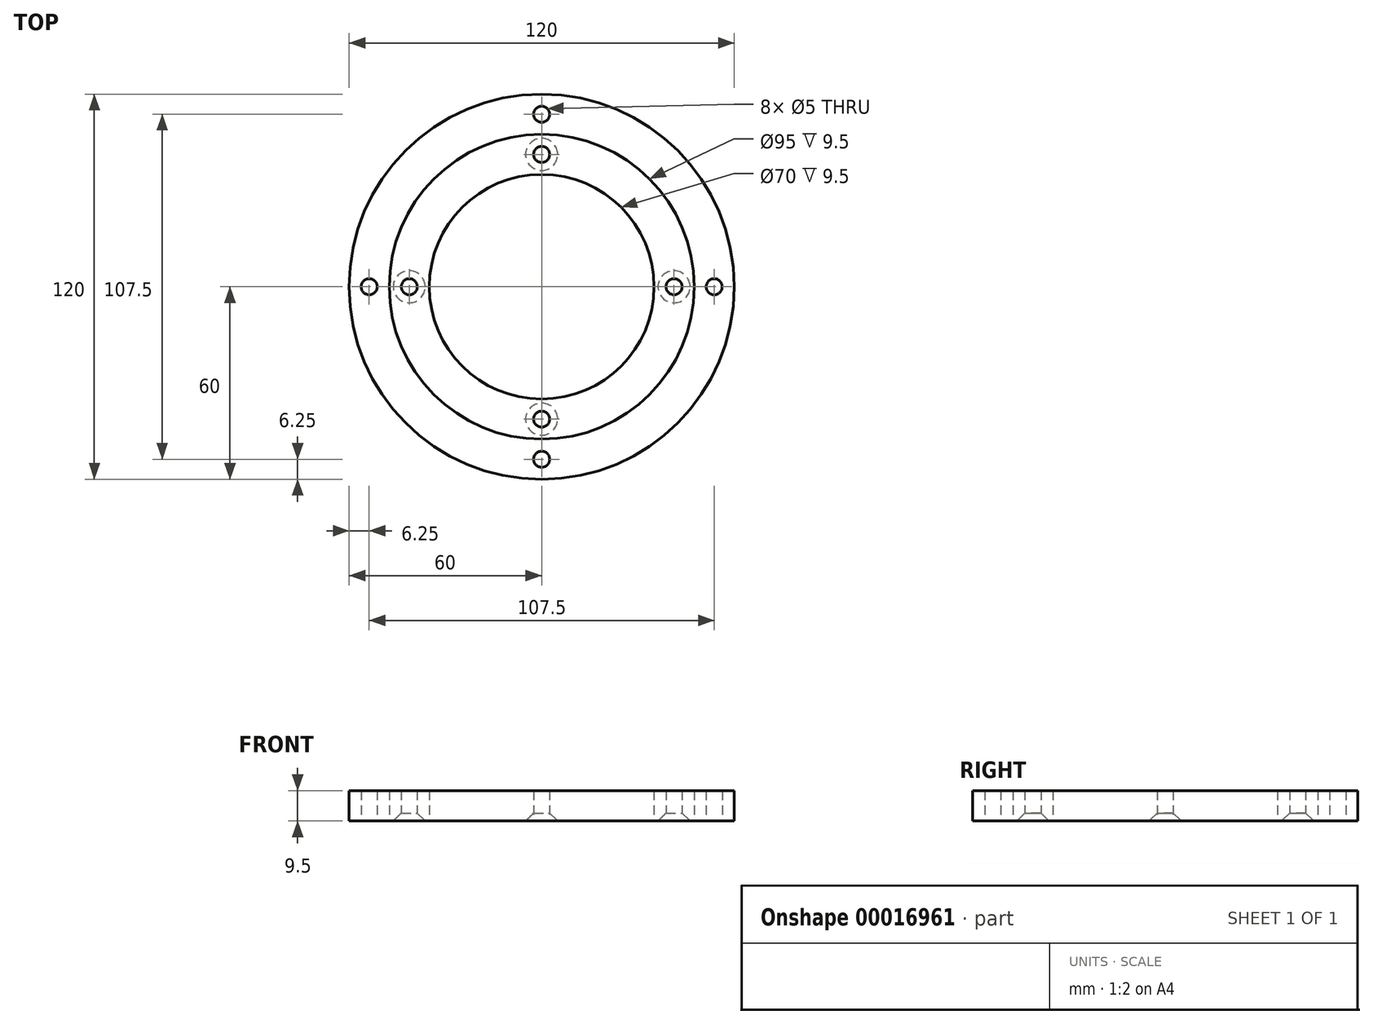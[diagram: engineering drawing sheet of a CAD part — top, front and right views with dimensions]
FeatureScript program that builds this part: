
annotation { "Feature Type Name" : "Feature", "Feature Type Description" : "" }
export const myFeature = defineFeature(function(context is Context, id is Id, definition is map)
    precondition{}
    {
        {
            var Q0;
            Q0=qCreatedBy(makeId("Top.planeOp"),FACE);
            var sketch = newSketch(context, id + "F0", { "sketchPlane" : qUnion([Q0])});
            skCircle(sketch, "E0", {"center": v(0, 0) * mm, "radius": 60 * mm});
            skCircle(sketch, "E1", {"center": v(0, 0) * mm, "radius": 47.5 * mm});
            skCircle(sketch, "E2", {"center": v(0, 0) * mm, "radius": 35 * mm});
            skCircle(sketch, "E3", {"center": v(0, 0) * mm, "radius": 41.25 * mm, "construction": true});
            skCircle(sketch, "E4", {"center": v(0, 0) * mm, "radius": 53.75 * mm, "construction": true});
            skLineSegment(sketch, "E5", {"start": v(0, 0) * mm, "end": v(0, 60) * mm, "construction": true});
            skLineSegment(sketch, "E6", {"start": v(0, 60) * mm, "end": v(0, 47.5) * mm, "construction": true});
            skLineSegment(sketch, "E7", {"start": v(0, 47.5) * mm, "end": v(0, 35) * mm, "construction": true});
            skPoint(sketch, "E8", {"position": v(0, 53.75) * mm});
            skPoint(sketch, "E9", {"position": v(0, 41.25) * mm});
            skPoint(sketch, "E10.1.0", {"position": v(-53.75, 0) * mm});
            skPoint(sketch, "E10.1.1", {"position": v(-41.25, 0) * mm});
            skPoint(sketch, "E10.2.0", {"position": v(0, -53.75) * mm});
            skPoint(sketch, "E10.2.1", {"position": v(0, -41.25) * mm});
            skPoint(sketch, "E10.3.0", {"position": v(53.75, 0) * mm});
            skPoint(sketch, "E10.3.1", {"position": v(41.25, 0) * mm});
            skSolve(sketch);
        }
        {
            var Q0;
            Q0=makeQuery(id+"F0.imprint","IMPRINT",FACE,{"disambiguationData":[TD([[makeQuery(id+"F0.imprint","IMPRINT",EDGE,{"derivedFrom":sQuery(id+"F0.wireOp",EDGE,"E1")}),1.0]])]});
            extrude(context, id + "F1", {"entities" : qUnion([Q0]), "depth" : 9.5 * mm});
        }
        {
            var Q0;
            Q0=makeQuery(id+"F0.imprint","IMPRINT",FACE,{"disambiguationData":[TD([[makeQuery(id+"F0.imprint","IMPRINT",EDGE,{"derivedFrom":sQuery(id+"F0.wireOp",EDGE,"E0")}),1.0]])]});
            extrude(context, id + "F2", {"entities" : qUnion([Q0]), "depth" : 9.5 * mm});
        }
        {
            var Q0;
            Q0=sQuery(id+"F0.wireOp",VERTEX,"E9");
            var Q1;
            Q1=makeQuery(id+"F1.opExtrude","SWEPT_BODY",BODY,{"disambiguationData":[OSD([sQuery(id+"F0.wireOp",EDGE,"E1"),sQuery(id+"F0.wireOp",EDGE,"E2")])]});
            hole(context, id + "F3", {"style" : HoleStyle.C_SINK, "holeDiameter" : 5 * mm, "cSinkDiameter" : 10 * mm, "endStyle" : HoleEndStyle.THROUGH, "oppositeDirection" : true, "locations" : qUnion([Q0]), "scope" : qUnion([Q1]), "cSinkAngle" : 90 * degree});
        }
        {
            var Q0;
            Q0=sQuery(id+"F0.wireOp",VERTEX,"E10.3.1");
            var Q1;
            Q1=sQuery(id+"F0.wireOp",VERTEX,"E10.2.1");
            var Q2;
            Q2=sQuery(id+"F0.wireOp",VERTEX,"E10.1.1");
            var Q3;
            Q3=makeQuery(id+"F1.opExtrude","SWEPT_BODY",BODY,{"disambiguationData":[OSD([sQuery(id+"F0.wireOp",EDGE,"E1"),sQuery(id+"F0.wireOp",EDGE,"E2")])]});
            hole(context, id + "F4", {"style" : HoleStyle.C_SINK, "holeDiameter" : 5 * mm, "cSinkDiameter" : 10 * mm, "endStyle" : HoleEndStyle.THROUGH, "oppositeDirection" : true, "locations" : qUnion([Q0, Q1, Q2]), "scope" : qUnion([Q3]), "cSinkAngle" : 90 * degree});
        }
        {
            var Q0;
            Q0=sQuery(id+"F0.wireOp",VERTEX,"E8");
            var Q1;
            Q1=sQuery(id+"F0.wireOp",VERTEX,"E10.3.0");
            var Q2;
            Q2=sQuery(id+"F0.wireOp",VERTEX,"E10.1.0");
            var Q3;
            Q3=sQuery(id+"F0.wireOp",VERTEX,"E10.2.0");
            var Q4;
            Q4=makeQuery(id+"F2.opExtrude","SWEPT_BODY",BODY,{"disambiguationData":[OSD([sQuery(id+"F0.wireOp",EDGE,"E0"),sQuery(id+"F0.wireOp",EDGE,"E1")])]});
            hole(context, id + "F5", {"style" : HoleStyle.SIMPLE, "holeDiameter" : 5 * mm, "endStyle" : HoleEndStyle.THROUGH, "oppositeDirection" : true, "locations" : qUnion([Q0, Q1, Q2, Q3]), "scope" : qUnion([Q4])});
        }
    });
